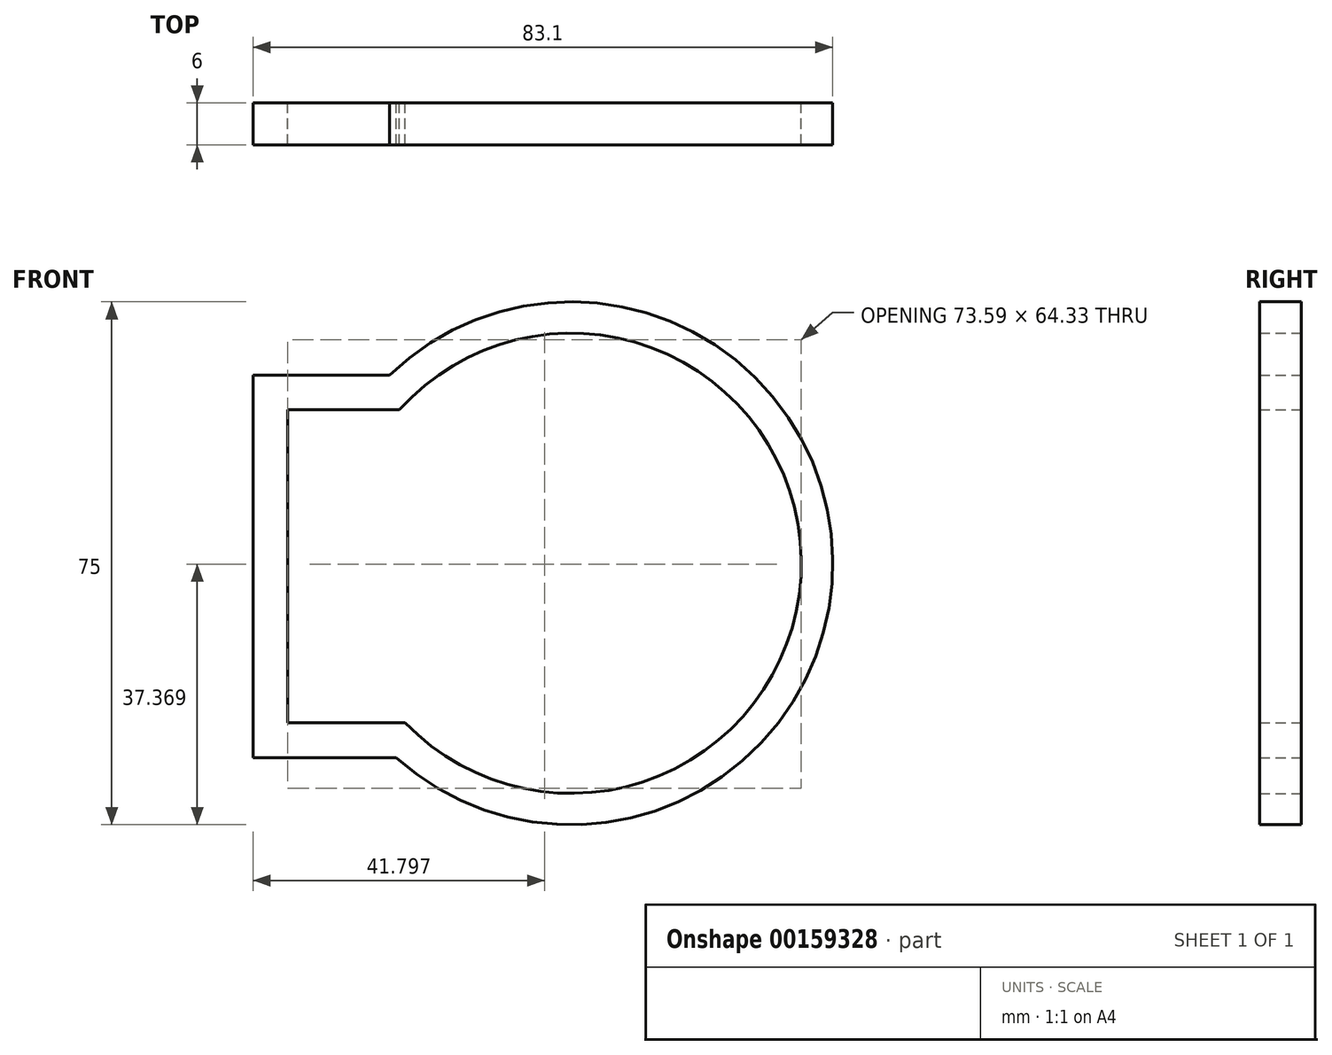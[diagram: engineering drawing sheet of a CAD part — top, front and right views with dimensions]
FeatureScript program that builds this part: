
annotation { "Feature Type Name" : "Feature", "Feature Type Description" : "" }
export const myFeature = defineFeature(function(context is Context, id is Id, definition is map)
    precondition{}
    {
        {
            var Q0;
            Q0=qCreatedBy(makeId("Front.planeOp"),FACE);
            var sketch = newSketch(context, id + "F0", { "sketchPlane" : qUnion([Q0])});
            skLineSegment(sketch, "E0.bottom", {"start": v(-28, 22) * mm, "end": v(-12, 22) * mm});
            skLineSegment(sketch, "E0.top", {"start": v(-28, -22.86) * mm, "end": v(-11.2, -22.86) * mm});
            skLineSegment(sketch, "E0.left", {"start": v(-28, 22) * mm, "end": v(-28, -22.86) * mm});
            skArc(sketch, "E1", {"start": v(-11.2, -22.86) * mm, "mid": v(45.6, 0.59) * mm, "end": v(-12, 22) * mm});
            skArc(sketch, "E2", {"start": v(-12.5, -27.86) * mm, "mid": v(50.1, 0.63) * mm, "end": v(-13.43, 27) * mm});
            skLineSegment(sketch, "E3", {"start": v(-13.43, 27) * mm, "end": v(-33, 27) * mm});
            skLineSegment(sketch, "E4", {"start": v(-33, 27) * mm, "end": v(-33, -27.86) * mm});
            skLineSegment(sketch, "E5", {"start": v(-33, -27.86) * mm, "end": v(-12.5, -27.86) * mm});
            skSolve(sketch);
        }
        {
            var Q0;
            Q0 = qSketchRegion(id + "F0", true);
            extrude(context, id + "F1", {"entities" : qUnion([Q0]), "depth" : 6 * mm});
        }
    });
